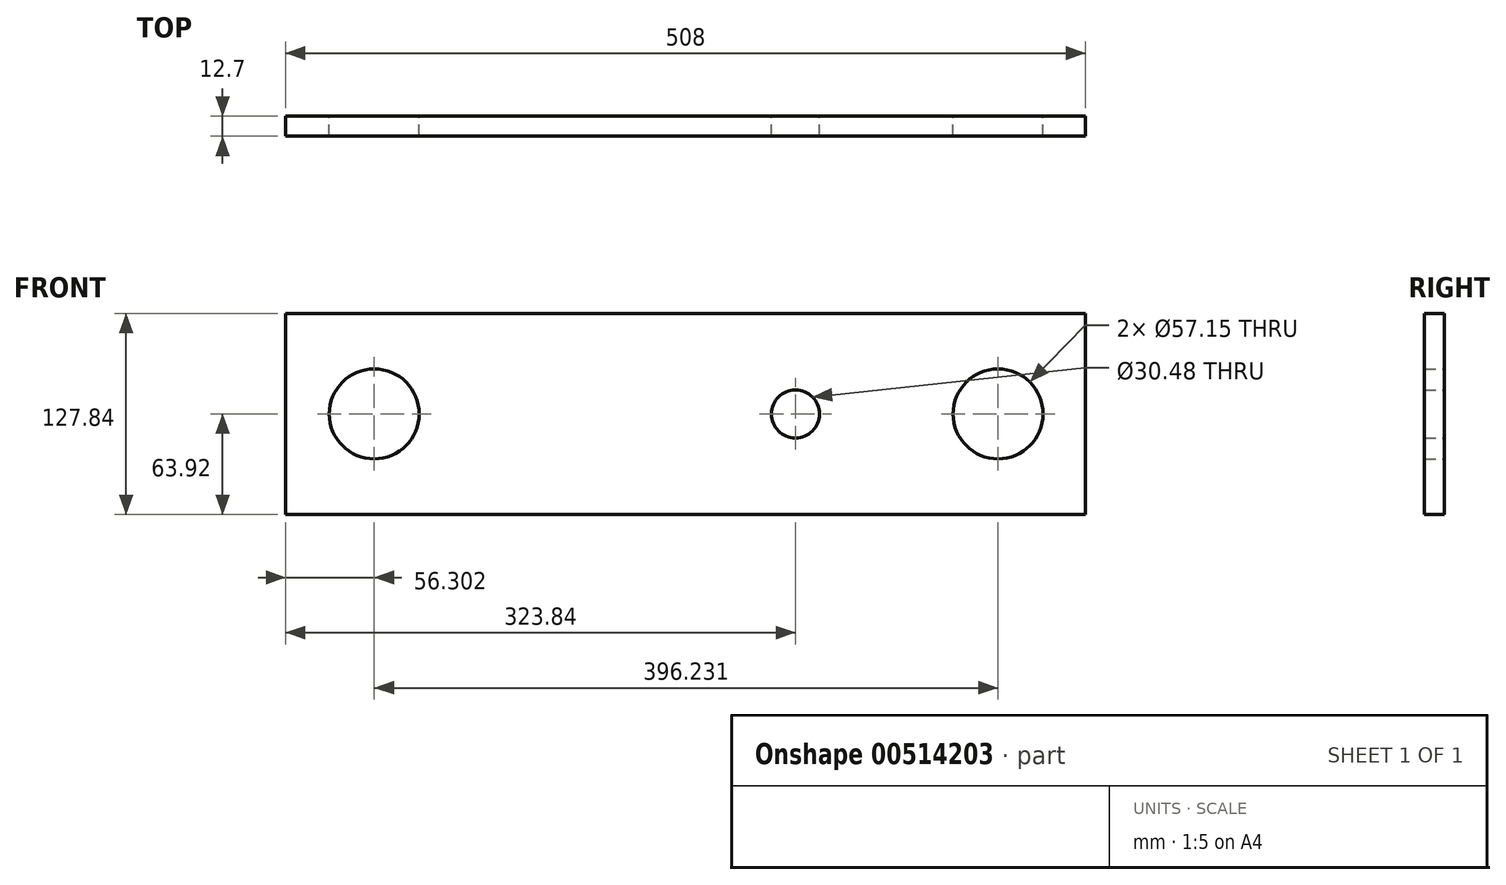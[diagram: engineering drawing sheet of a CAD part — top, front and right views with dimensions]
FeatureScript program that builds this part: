
annotation { "Feature Type Name" : "Feature", "Feature Type Description" : "" }
export const myFeature = defineFeature(function(context is Context, id is Id, definition is map)
    precondition{}
    {
        {
            var Q0;
            Q0=qCreatedBy(makeId("Front.planeOp"),FACE);
            var sketch = newSketch(context, id + "F0", { "sketchPlane" : qUnion([Q0])});
            skLineSegment(sketch, "E0.bottom", {"start": v(254, -63.92) * mm, "end": v(-254, -63.92) * mm});
            skLineSegment(sketch, "E0.top", {"start": v(254, 63.92) * mm, "end": v(-254, 63.92) * mm});
            skLineSegment(sketch, "E0.left", {"start": v(254, -63.92) * mm, "end": v(254, 63.92) * mm});
            skLineSegment(sketch, "E0.right", {"start": v(-254, -63.92) * mm, "end": v(-254, 63.92) * mm});
            skPoint(sketch, "E0.middle", {"position": v(0, 0) * mm});
            skSolve(sketch);
        }
        {
            var Q0;
            Q0 = qSketchRegion(id + "F0", true);
            extrude(context, id + "F1", {"entities" : qUnion([Q0]), "depth" : 12.7 * mm, "offsetDistance" : 25.4 * mm});
        }
        {
            var Q0;
            Q0=makeQuery(id+"F1.opExtrude","CAP_FACE",FACE,{"disambiguationData":[OSD([sQuery(id+"F0.wireOp",EDGE,"E0.bottom"),sQuery(id+"F0.wireOp",EDGE,"E0.top"),sQuery(id+"F0.wireOp",EDGE,"E0.left"),sQuery(id+"F0.wireOp",EDGE,"E0.right")])],"isStart":false});
            var sketch = newSketch(context, id + "F2", { "sketchPlane" : qUnion([Q0])});
            skCircle(sketch, "E1", {"center": v(-197.7, 0) * mm, "radius": 28.58 * mm});
            skCircle(sketch, "E2", {"center": v(198.53, 0) * mm, "radius": 28.58 * mm});
            skPoint(sketch, "E2.centerSnap0", {"position": v(254, 0) * mm});
            skSolve(sketch);
        }
        {
            var Q0;
            Q0=sQuery(id+"F2.wireOp",VERTEX,"E1.center");
            var Q1;
            Q1=sQuery(id+"F2.wireOp",VERTEX,"E2.center");
            var Q2;
            Q2=makeQuery(id+"F1.opExtrude","SWEPT_BODY",BODY,{"disambiguationData":[OSD([sQuery(id+"F0.wireOp",EDGE,"E0.bottom"),sQuery(id+"F0.wireOp",EDGE,"E0.top"),sQuery(id+"F0.wireOp",EDGE,"E0.left"),sQuery(id+"F0.wireOp",EDGE,"E0.right")])]});
            hole(context, id + "F3", {"style" : HoleStyle.SIMPLE, "endStyle" : HoleEndStyle.THROUGH, "holeDiameter" : 57.15 * mm, "isTappedThrough" : true, "tappedDepth" : 12.7 * mm, "tapClearance" : 3, "locations" : qUnion([Q0, Q1]), "scope" : qUnion([Q2])});
        }
        {
            var Q0;
            Q0=makeQuery(id+"F1.opExtrude","CAP_FACE",FACE,{"disambiguationData":[OSD([sQuery(id+"F0.wireOp",EDGE,"E0.bottom"),sQuery(id+"F0.wireOp",EDGE,"E0.top"),sQuery(id+"F0.wireOp",EDGE,"E0.left"),sQuery(id+"F0.wireOp",EDGE,"E0.right")])],"isStart":false});
            var sketch = newSketch(context, id + "F4", { "sketchPlane" : qUnion([Q0])});
            skCircle(sketch, "E3", {"center": v(69.84, 0) * mm, "radius": 19.05 * mm});
            skSolve(sketch);
        }
        {
            var Q0;
            Q0=sQuery(id+"F4.wireOp",VERTEX,"E3.center");
            var Q1;
            Q1=makeQuery(id+"F1.opExtrude","SWEPT_BODY",BODY,{"disambiguationData":[OSD([sQuery(id+"F0.wireOp",EDGE,"E0.bottom"),sQuery(id+"F0.wireOp",EDGE,"E0.top"),sQuery(id+"F0.wireOp",EDGE,"E0.left"),sQuery(id+"F0.wireOp",EDGE,"E0.right")])]});
            hole(context, id + "F5", {"style" : HoleStyle.SIMPLE, "endStyle" : HoleEndStyle.THROUGH, "holeDiameter" : 30.48 * mm, "isTappedThrough" : true, "tappedDepth" : 12.7 * mm, "tapClearance" : 3, "locations" : qUnion([Q0]), "scope" : qUnion([Q1])});
        }
    });
